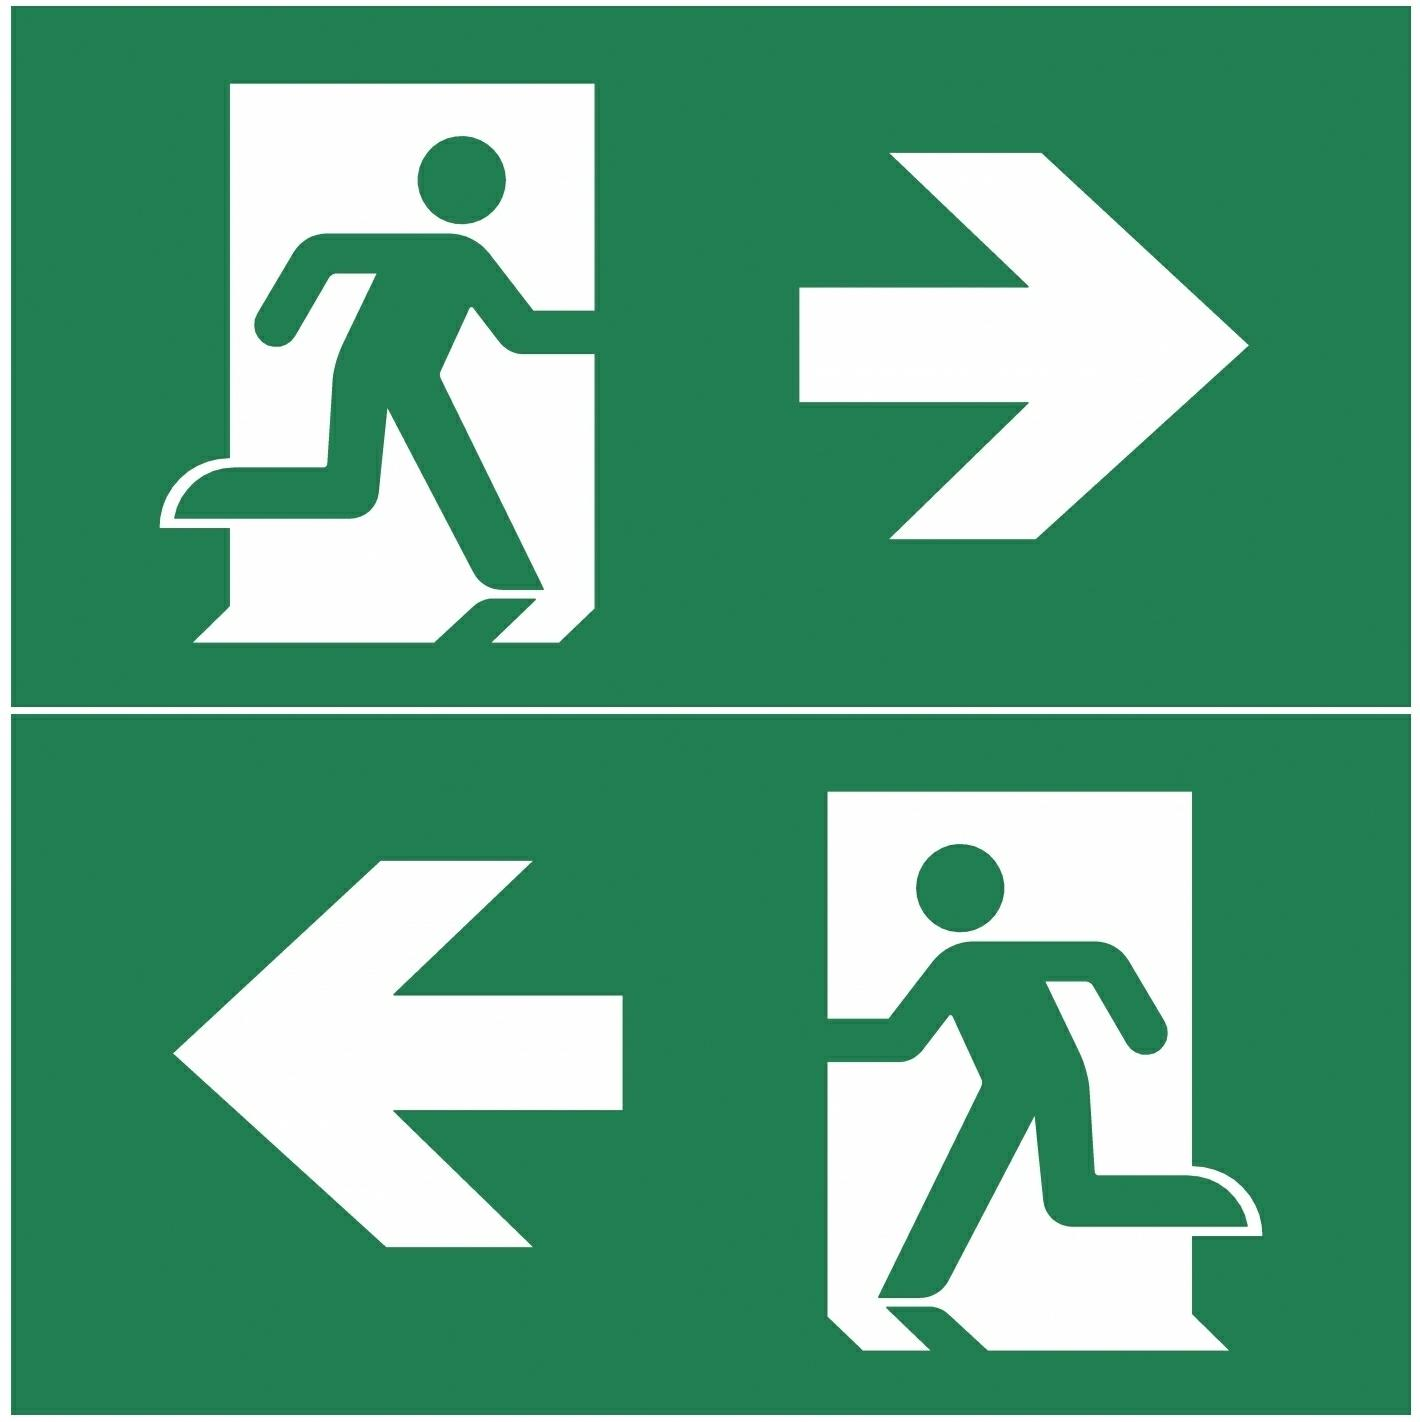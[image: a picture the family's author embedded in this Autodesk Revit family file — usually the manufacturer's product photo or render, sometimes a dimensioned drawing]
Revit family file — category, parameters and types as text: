
# Revit family: TWS8092WM
name_source: partatom
category: Lighting Fixtures
revit_build: Autodesk Revit 2016 (Build: 20150714_1515(x64)
units: mm (PartAtom-declared; Revit-internal decimal feet)

## family parameters
Always vertical = Yes
Cut with Voids When Loaded = No
Light Source = No
OmniClass Number = 23.80.70.00
OmniClass Title = Lighting
Part Type = Normal
Room Calculation Point = No
Round Connector Dimension = Use Diameter
Shared = No
Work Plane-Based = No

## types (6) — shared parameters
Aperture for Recess Mounting = 53 mm x 275 mm
Body Material = Plastic
Color = RAL9003
Customs Code = 94056080
Description = Self-Contained LED Exit Light with 1 h Super Capacitor Backup and Self Testing
ETIM Product Class = EC001957
Electrical Installation = 2/3 x 2,5 mm² -o-
Feature = ESCAP, Lumi Test
GTIN Code = 6438045011875
Glow Wire Test of Plastic Materials = 650 °C
Height = 185 mm  [stored 0.606955 ft]
IP Class = IP44
Keynote = 23
Length = 268 mm  [stored 0.879265 ft]
Light Source = LED
Manufacturer = Teknoware Oy
Max Input Power VA = 4 VA
Model = ESC 80
Mounting_Optional = Recess, Flag, Pendel
Mounting_Standard = Wall, Ceiling
Nominal Supply Voltage = 220-240 V, 50/60 Hz AC
Product Code = TWS8092WM
Protection Class = II
Sähkönumero = 4211323
Sähkönumerot.fi -tuotesivu = http://www.sahkonumerot.fi
Type Image = ESC80.jpg
URL = http://www.teknoware.com
Viewing Distance = 20000 mm  [stored 65.6168 ft]
Wattage Comments = LED
Weight = 0.80 kg
Width = 40 mm  [stored 0.131234 ft]

## per-type parameters (varying)
| type | Max Input Power W | Pictogram Type | Temperature Range Min_Max |
| Arrow down 20m | 0 W | OPASTE PBV80202E | -25...+35 °C |
| Arrow down 30m | 0 W | OPASTE PBV80302E | -5...+30 °C |
| Arrow down 26m | 0 W | OPASTE PBV80262E | -5...+30 °C |
| Arrow left_right 20m | 0 W | OPASTE PBV80201E | -5...+30 °C |
| Arrow left_right 26m | 4 W | OPASTE PBV80261E | -5...+30 °C |
| Arrow left_right 30m | 0 W | OPASTE PBV80301E | -5...+30 °C |

note: [stored X ft] marks values corroborated as IEEE doubles in the binary element streams (Revit-internal decimal feet)

## geometry (parser evidence)
native form markers: Sweep x24
no freeform markers — native parametric forms only
